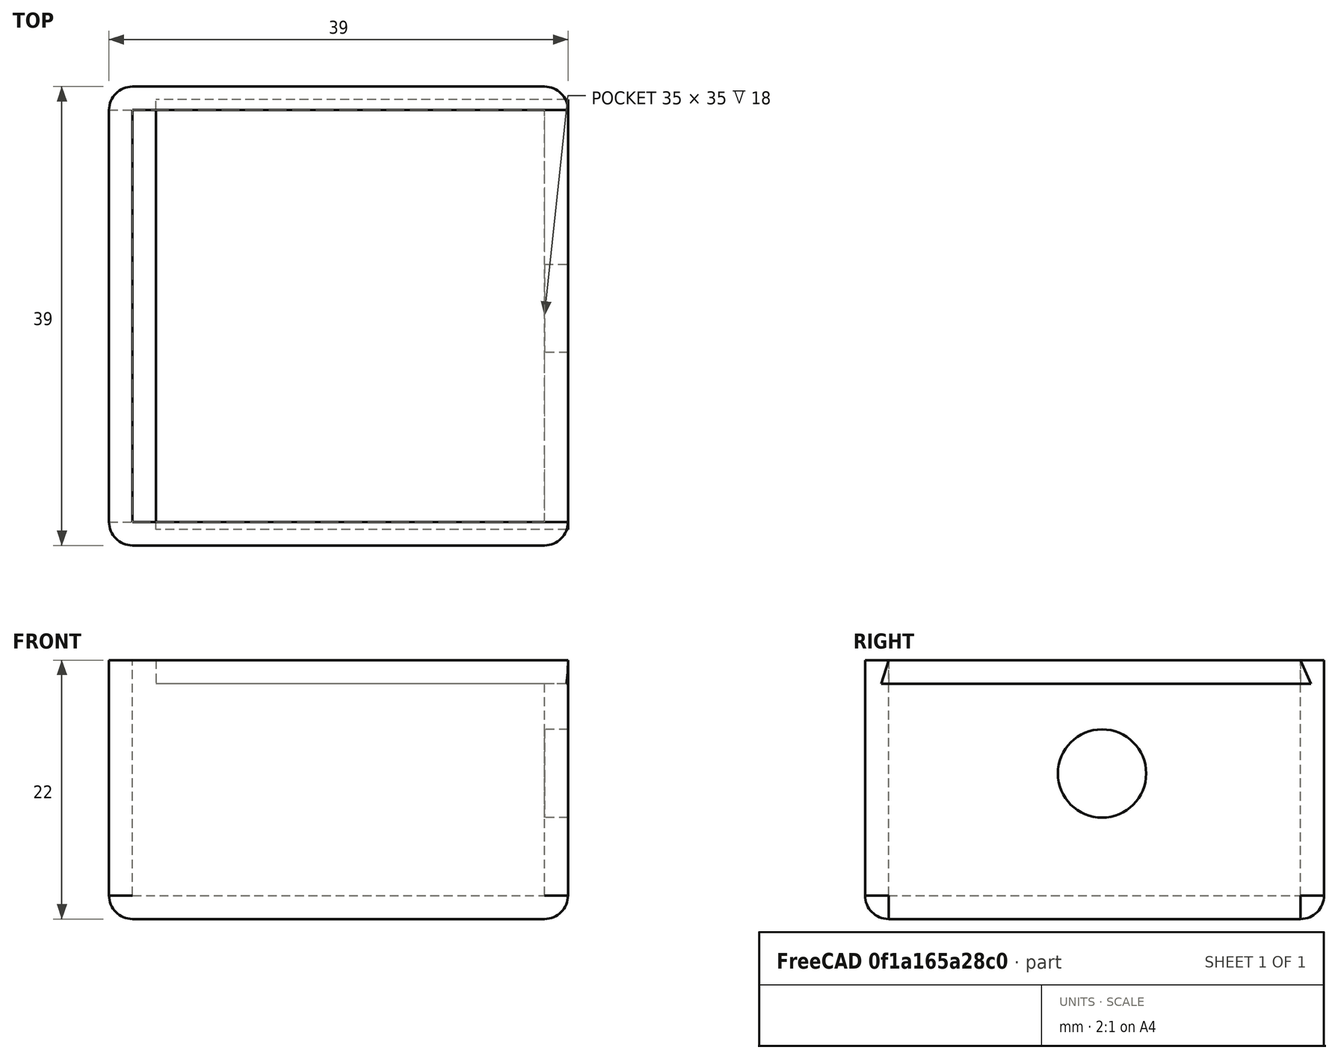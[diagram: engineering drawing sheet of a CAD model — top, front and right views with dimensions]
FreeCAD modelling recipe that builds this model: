
FCSTD DOCUMENT  (FreeCAD 0.20R29603 (Git))
Label: controlerBoxSmall
License: All rights reserved
LicenseURL: http://en.wikipedia.org/wiki/All_rights_reserved
objects: Sketcher::SketchObject×2, Part::Extrusion×2, Part::Cut×2, Part::Box×1, Part::Thickness×1, Part::FeaturePython×1
note: 9 computed .brp shape members not serialized (recipe doc carries the construction recipe); baked Part::Feature solids carry a one-line shape summary decoded from their .brp

FEATURE [Part::Box] Box  label="Cube"
  AttacherType = Attacher::AttachEngine3D
  Height = 20
  Length = 35
  Width = 35
FEATURE [Part::Thickness] Thickness  label="box001"
  Faces = -> Box [Face6]
  Intersection = false
  Join = 0
  Mode = 0
  SelfIntersection = false
  Value = 2
FEATURE [Sketcher::SketchObject] Sketch001
  FullyConstrained = false
  MapMode = 5
  Placement = pos=(37,0,0) rot=(0.57735,0.57735,0.57735;2.0944rad)
  sketch-geometry (3):
    g0: LineSegment StartX=35 StartY=20 StartZ=0 EndX=0 EndY=0 EndZ=0
    g1: LineSegment StartX=0 StartY=20 StartZ=0 EndX=35 EndY=0 EndZ=0
    g2: Circle CenterX=18.1382 CenterY=10.3647 CenterZ=0 NormalX=0 NormalY=0 NormalZ=1 AngleXU=0 Radius=3.75
  constraints (2):
    c: PointOnObject(g2,g0)
    c: Diameter(g2) = 7.5
FEATURE [Part::Extrusion] Extrude001  label="hole"
  Base = -> Sketch001
  Dir = (1,0,0)
  DirMode = 0
  FaceMakerClass = Part::FaceMakerBullseye
  LengthFwd = 4.5
  LengthRev = 0
  Solid = true
  Symmetric = true
FEATURE [Sketcher::SketchObject] Sketch002
  AttachmentOffset = pos=(0,-15,0) rot=(0,-0.994505,-0.104685;0rad)
  ExternalGeometry = -> [Thickness]
  FullyConstrained = false
  MapMode = 5
  Placement = pos=(37,0,-15) rot=(0.57735,0.57735,0.57735;2.0944rad)
  Support = -> [Thickness]
  sketch-geometry (4):
    g0: LineSegment StartX=-0.633947 StartY=33 StartZ=0 EndX=35.8886 EndY=33 EndZ=0
    g1: LineSegment StartX=35 StartY=35 StartZ=0 EndX=35.8886 EndY=33 EndZ=0
    g2: LineSegment StartX=0 StartY=35 StartZ=0 EndX=-0.633947 EndY=33 EndZ=0
    g3: LineSegment StartX=0 StartY=35 StartZ=0 EndX=35 EndY=35 EndZ=0
  constraints (5):
    c: Horizontal(g0)
    c: Coincident(g1,g0)
    c: Coincident(g2,g0)
    c: Coincident(g3,g2)
    c: Coincident(g3,g1)
FEATURE [Part::Extrusion] Extrude002
  Base = -> Sketch002
  Dir = (1,0,0)
  DirMode = 0
  FaceMakerClass = Part::FaceMakerBullseye
  LengthFwd = 35
  LengthRev = 0
  Reversed = true
  Solid = true
  Symmetric = false
  expr: LengthFwd = <<Cube>>.Length
FEATURE [Part::FeaturePython] Clone  label="cover"  # Draft clone (typed FeaturePython)
  AttacherType = Attacher::AttachEngine3D
  Fuse = false
  Objects = -> [Extrude002]
  Scale = (1,1,1)
FEATURE [Part::Cut] Cut
  Base = -> Thickness
  Tool = -> Extrude001
FEATURE [Part::Cut] Cut001  label="finalbox"
  Base = -> Cut
  Tool = -> Extrude002
